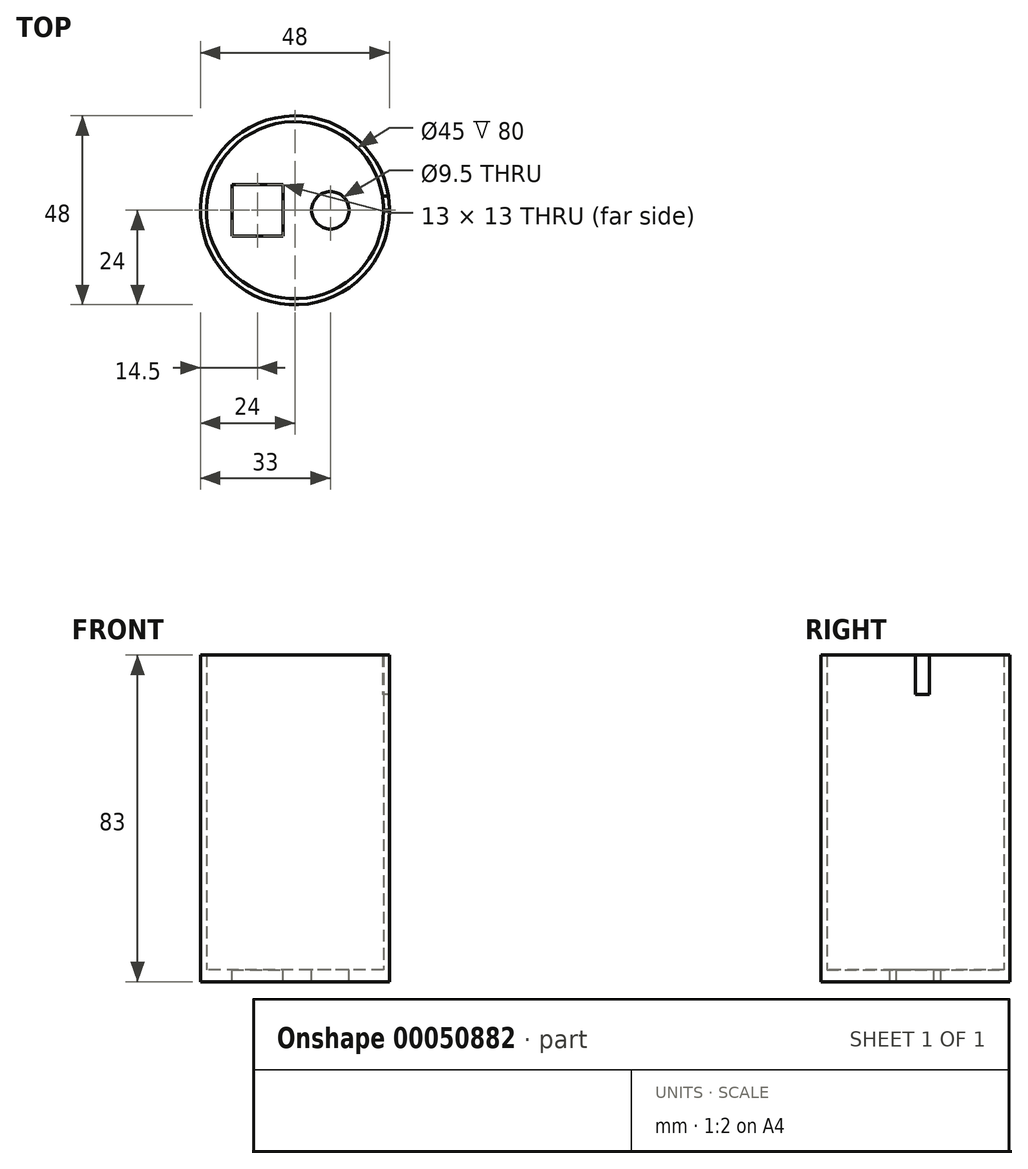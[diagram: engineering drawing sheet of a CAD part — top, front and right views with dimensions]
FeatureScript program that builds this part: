
annotation { "Feature Type Name" : "Feature", "Feature Type Description" : "" }
export const myFeature = defineFeature(function(context is Context, id is Id, definition is map)
    precondition{}
    {
        {
            var Q0;
            Q0=qCreatedBy(makeId("Top.planeOp"),FACE);
            var sketch = newSketch(context, id + "F0", { "sketchPlane" : qUnion([Q0])});
            skCircle(sketch, "E0", {"center": v(0, 0) * mm, "radius": 24 * mm});
            skSolve(sketch);
        }
        {
            var Q0;
            Q0=makeQuery(id+"F0.imprint","IMPRINT",FACE,{"disambiguationData":[TD([[makeQuery(id+"F0.imprint","IMPRINT",EDGE,{"derivedFrom":sQuery(id+"F0.wireOp",EDGE,"E0")}),1.0]])]});
            extrude(context, id + "F1", {"entities" : qUnion([Q0]), "depth" : 3 * mm});
        }
        {
            var Q0;
            Q0=makeQuery(id+"F1.opExtrude","CAP_FACE",FACE,{"disambiguationData":[OSD([sQuery(id+"F0.wireOp",EDGE,"E0")])],"isStart":false});
            var sketch = newSketch(context, id + "F2", { "sketchPlane" : qUnion([Q0])});
            skCircle(sketch, "E1", {"center": v(0, 0) * mm, "radius": 22.5 * mm});
            skSolve(sketch);
        }
        {
            var Q0;
            Q0=makeQuery(id+"F2.imprint","IMPRINT",FACE,{"disambiguationData":[TD([[makeQuery(id+"F2.imprint","IMPRINT",EDGE,{"derivedFrom":sQuery(id+"F2.wireOp",EDGE,"E1")}),-1.0]])]});
            extrude(context, id + "F3", {"entities" : qUnion([Q0]), "operationType" : NewBodyOperationType.ADD, "depth" : 80 * mm});
        }
        {
            var Q0;
            Q0=makeQuery(id+"F1.opExtrude","CAP_FACE",FACE,{"disambiguationData":[OSD([sQuery(id+"F0.wireOp",EDGE,"E0")])],"isStart":false});
            var sketch = newSketch(context, id + "F4", { "sketchPlane" : qUnion([Q0])});
            skCircle(sketch, "E2", {"center": v(9, 0) * mm, "radius": 4.75 * mm});
            skLineSegment(sketch, "E3.bottom", {"start": v(-16, 6.5) * mm, "end": v(-3, 6.5) * mm});
            skLineSegment(sketch, "E3.top", {"start": v(-16, -6.5) * mm, "end": v(-3, -6.5) * mm});
            skLineSegment(sketch, "E3.left", {"start": v(-16, 6.5) * mm, "end": v(-16, -6.5) * mm});
            skLineSegment(sketch, "E3.right", {"start": v(-3, 6.5) * mm, "end": v(-3, -6.5) * mm});
            skSolve(sketch);
        }
        {
            var Q0;
            Q0=makeQuery(id+"F4.imprint","IMPRINT",FACE,{"disambiguationData":[TD([[makeQuery(id+"F4.imprint","IMPRINT",EDGE,{"derivedFrom":sQuery(id+"F4.wireOp",EDGE,"E3.bottom")}),-1.0]])]});
            var Q1;
            Q1=makeQuery(id+"F4.imprint","IMPRINT",FACE,{"disambiguationData":[TD([[makeQuery(id+"F4.imprint","IMPRINT",EDGE,{"derivedFrom":sQuery(id+"F4.wireOp",EDGE,"E2")}),1.0]])]});
            extrude(context, id + "F5", {"entities" : qUnion([Q0, Q1]), "operationType" : NewBodyOperationType.REMOVE, "endBound" : BoundingType.THROUGH_ALL, "oppositeDirection" : true, "depth" : 3 * mm});
        }
        {
            var Q0;
            Q0=qCreatedBy(makeId("Right.planeOp"),FACE);
            var sketch = newSketch(context, id + "F6", { "sketchPlane" : qUnion([Q0])});
            skLineSegment(sketch, "E4.bottom", {"start": v(0, 83) * mm, "end": v(3.55, 83) * mm});
            skLineSegment(sketch, "E4.top", {"start": v(0, 73) * mm, "end": v(3.55, 73) * mm});
            skLineSegment(sketch, "E4.left", {"start": v(0, 83) * mm, "end": v(0, 73) * mm});
            skLineSegment(sketch, "E4.right", {"start": v(3.55, 83) * mm, "end": v(3.55, 73) * mm});
            skSolve(sketch);
        }
        {
            var Q0;
            Q0 = qSketchRegion(id + "F6", true);
            extrude(context, id + "F7", {"entities" : qUnion([Q0]), "operationType" : NewBodyOperationType.REMOVE, "depth" : 25 * mm});
        }
    });
